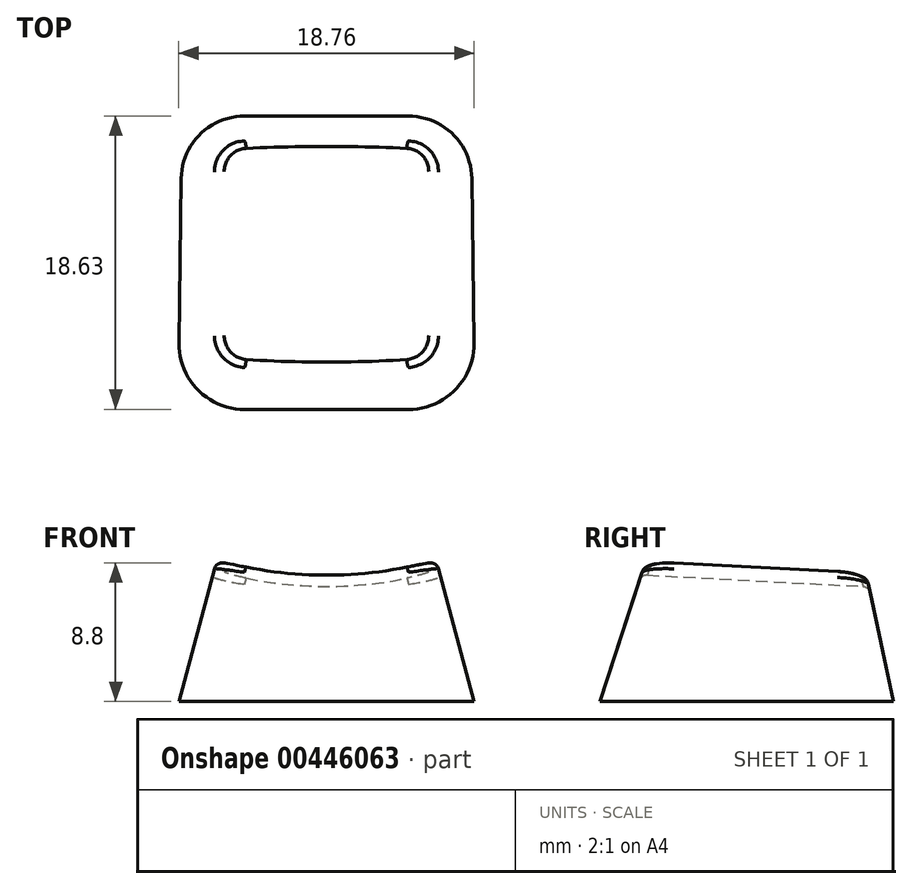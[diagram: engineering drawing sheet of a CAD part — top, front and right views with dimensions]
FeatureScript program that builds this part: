
annotation { "Feature Type Name" : "Feature", "Feature Type Description" : "" }
export const myFeature = defineFeature(function(context is Context, id is Id, definition is map)
    precondition{}
    {
        {
            var Q0;
            Q0=qCreatedBy(makeId("Top.planeOp"),FACE);
            var sketch = newSketch(context, id + "F0", { "sketchPlane" : qUnion([Q0])});
            skLineSegment(sketch, "E0.bottom", {"start": v(5.2, -6.99) * mm, "end": v(-5.2, -6.99) * mm});
            skLineSegment(sketch, "E0.top", {"start": v(5.2, 6.99) * mm, "end": v(-5.2, 6.99) * mm});
            skLineSegment(sketch, "E0.left", {"start": v(6.99, -5.2) * mm, "end": v(6.99, 5.2) * mm});
            skLineSegment(sketch, "E0.right", {"start": v(-6.99, -5.2) * mm, "end": v(-6.99, 5.2) * mm});
            skPoint(sketch, "E0.middle", {"position": v(0, 0) * mm});
            skPoint(sketch, "E1.visualSharp", {"position": v(-6.99, 6.99) * mm});
            skArc(sketch, "E1.filletArc", {"start": v(-5.2, 6.99) * mm, "mid": v(-6.46, 6.46) * mm, "end": v(-6.99, 5.2) * mm});
            skPoint(sketch, "E2.visualSharp", {"position": v(6.99, 6.99) * mm});
            skArc(sketch, "E2.filletArc", {"start": v(6.99, 5.2) * mm, "mid": v(6.46, 6.46) * mm, "end": v(5.2, 6.99) * mm});
            skPoint(sketch, "E3.visualSharp", {"position": v(6.99, -6.99) * mm});
            skArc(sketch, "E3.filletArc", {"start": v(5.2, -6.99) * mm, "mid": v(6.46, -6.46) * mm, "end": v(6.99, -5.2) * mm});
            skPoint(sketch, "E4.visualSharp", {"position": v(-6.99, -6.99) * mm});
            skArc(sketch, "E4.filletArc", {"start": v(-6.99, -5.2) * mm, "mid": v(-6.46, -6.46) * mm, "end": v(-5.2, -6.99) * mm});
            skSolve(sketch);
        }
        {
            var Q0;
            Q0 = qSketchRegion(id + "F0", true);
            extrude(context, id + "F1", {"entities" : qUnion([Q0]), "oppositeDirection" : true, "depth" : 9.14 * mm, "offsetDistance" : 25.4 * mm, "hasDraft" : true, "draftAngle" : 15 * degree});
        }
        {
            var Q0;
            Q0=qCreatedBy(makeId("Front.planeOp"),FACE);
            var sketch = newSketch(context, id + "F2", { "sketchPlane" : qUnion([Q0])});
            skCircle(sketch, "E5", {"center": v(0, 24.42) * mm, "radius": 25.4 * mm});
            skSolve(sketch);
        }
        {
            var Q0;
            Q0 = qSketchRegion(id + "F2", true);
            extrude(context, id + "F3", {"entities" : qUnion([Q0]), "operationType" : NewBodyOperationType.REMOVE, "endBound" : BoundingType.SYMMETRIC, "depth" : 25.4 * mm, "offsetDistance" : 25.4 * mm});
        }
        {
            var Q0;
            Q0=makeQuery(id+"F3.boolean.opBoolean","INTERSECT",EDGE,{"derivedFrom":[makeQuery(id+"F1.opExtrude","SWEPT_FACE",FACE,{"disambiguationData":[OSD([sQuery(id+"F0.wireOp",EDGE,"E0.bottom")])]}),makeQuery(id+"F3.opExtrude","SWEPT_FACE",FACE,{"disambiguationData":[OSD([sQuery(id+"F2.wireOp",EDGE,"E5")])]})]});
            fillet(context, id + "F4", {"entities" : qUnion([Q0]), "tangentPropagation" : true, "radius" : 0.5 * mm, "defaultsChanged" : true, "vertexSettings" : [], "allowEdgeOverflow" : false});
        }
        {
            var Q0;
            Q0=qCreatedBy(makeId("Top.planeOp"),FACE);
            var sketch = newSketch(context, id + "F5", { "sketchPlane" : qUnion([Q0])});
            skLineSegment(sketch, "E6", {"start": v(0, 0) * mm, "end": v(16.12, 0) * mm, "construction": true});
            skSolve(sketch);
        }
        {
            var Q0;
            Q0=makeQuery(id+"F1.opExtrude","SWEPT_BODY",BODY,{"disambiguationData":[OSD([sQuery(id+"F0.wireOp",EDGE,"E0.bottom"),sQuery(id+"F0.wireOp",EDGE,"E0.top"),sQuery(id+"F0.wireOp",EDGE,"E0.left"),sQuery(id+"F0.wireOp",EDGE,"E0.right"),sQuery(id+"F0.wireOp",EDGE,"E1.filletArc"),sQuery(id+"F0.wireOp",EDGE,"E2.filletArc"),sQuery(id+"F0.wireOp",EDGE,"E3.filletArc"),sQuery(id+"F0.wireOp",EDGE,"E4.filletArc")])]});
            var Q1;
            Q1=sQuery(id+"F5.wireOp",EDGE,"E6");
            transform(context, id + "F6", {"entities" : qUnion([Q0]), "transformType" : TransformType.ROTATION, "transformAxis" : qUnion([Q1]), "angle" : 3 * degree, "oppositeDirection" : true, "makeCopy" : false});
        }
        {
            var Q0;
            Q0=qCreatedBy(makeId("Right.planeOp"),FACE);
            var sketch = newSketch(context, id + "F7", { "sketchPlane" : qUnion([Q0])});
            skLineSegment(sketch, "E7", {"start": v(-9.9, -8.64) * mm, "end": v(8.73, -8.64) * mm});
            skLineSegment(sketch, "E8", {"start": v(8.73, -8.64) * mm, "end": v(8.94, -9.63) * mm});
            skLineSegment(sketch, "E9", {"start": v(8.94, -9.63) * mm, "end": v(-9.9, -8.64) * mm});
            skSolve(sketch);
        }
        {
            var Q0;
            Q0 = qSketchRegion(id + "F7", true);
            extrude(context, id + "F8", {"entities" : qUnion([Q0]), "operationType" : NewBodyOperationType.REMOVE, "endBound" : BoundingType.SYMMETRIC, "depth" : 25.4 * mm, "offsetDistance" : 25.4 * mm});
        }
    });
